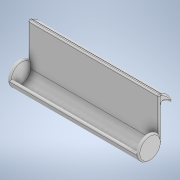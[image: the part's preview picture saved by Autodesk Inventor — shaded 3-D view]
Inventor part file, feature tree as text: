
AUTODESK INVENTOR PART (.ipt)
format: ipt  version: 2020 (Build 240168000, 168)  size: 245,248 bytes
history: native  units: in
note: dims shown in document units (in); Inventor stores cm internally (conversion verified against a paired STEP export)
features: extrude x3, fillet x3, sketch x3
ambient origin geometry x8: Origin, YZ Plane, XZ Plane, XY Plane, X Axis, Y Axis, Z Axis, Center Point
bodies: Solid1 (feature_tree)
feature tree (9):
  extrude  "Extrusion1"  Depth=1.1811in
  extrude  "Extrusion2"  Depth=0.1969in
  extrude  "Extrusion3"  Depth=0.0354in
  fillet  "Fillet1"  Radius=0.7087in
  fillet  "Fillet2"  Radius=0.0394in
  fillet  "Fillet3"  Radius=3.7795in
  sketch  "Sketch1"  dims[d0=0.6693in d1=1.1811in]
  sketch  "Sketch2"  dims[d2=0.0787in d3=0.1969in]
  sketch  "Sketch3"  dims[d4=0.3937in d6=0.5906in d7=0.7087in d8=0.0394in d9=3.7795in d10=0.0in d11=0.0787in d12=0.0in d13=0.0787in d14=0.0in d15=0.0197in d16=0.0394in d17=0.0354in]
